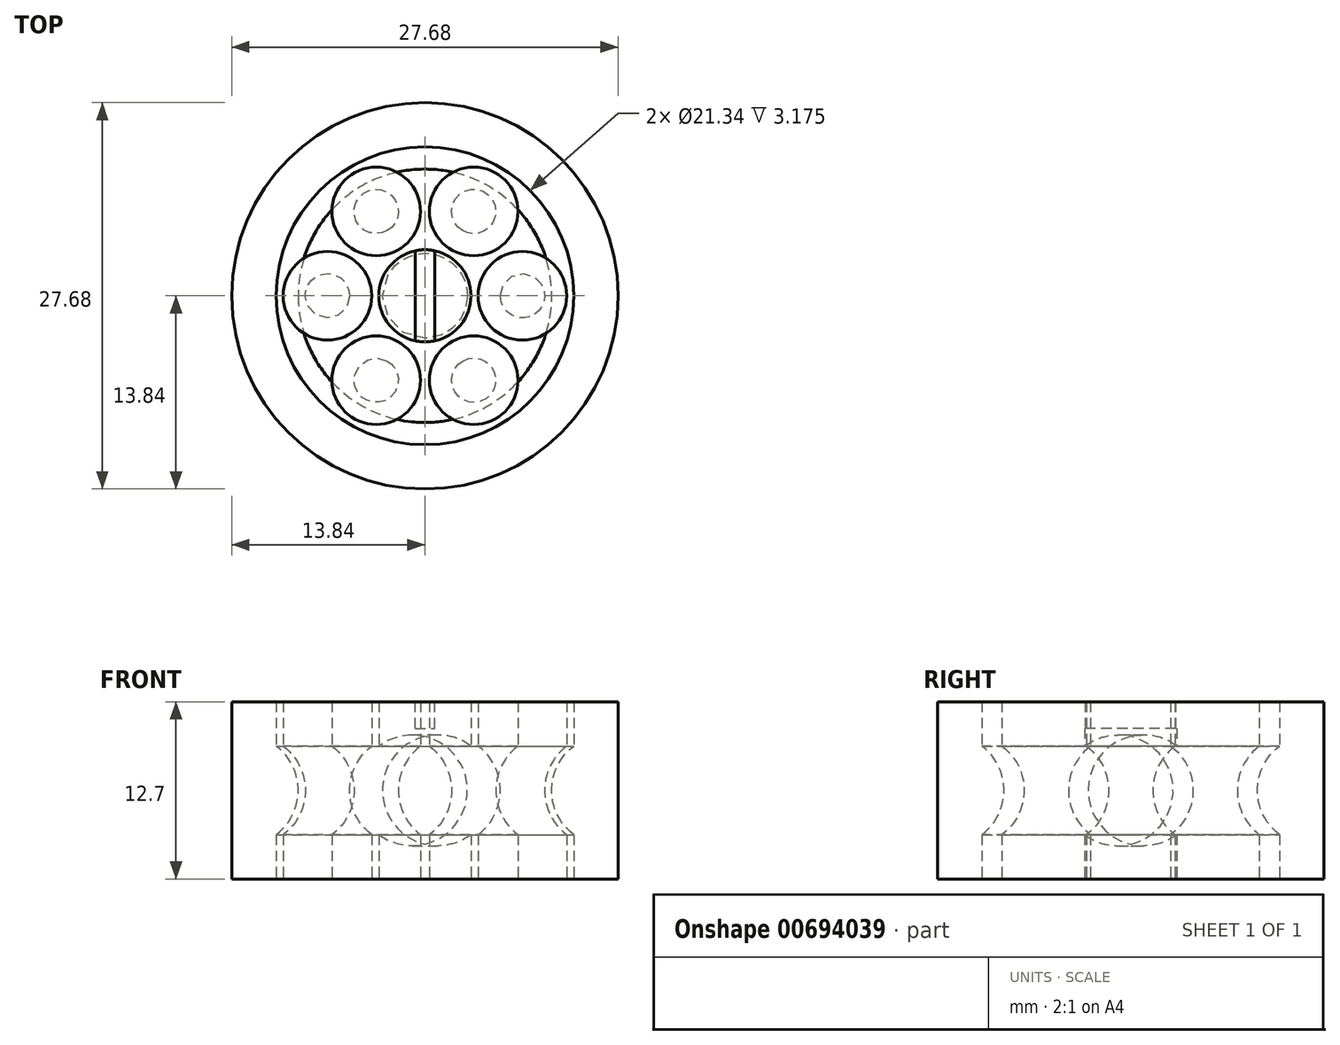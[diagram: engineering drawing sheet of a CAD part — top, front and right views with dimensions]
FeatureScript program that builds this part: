
annotation { "Feature Type Name" : "Feature", "Feature Type Description" : "" }
export const myFeature = defineFeature(function(context is Context, id is Id, definition is map)
    precondition{}
    {
        {
            var Q0;
            Q0=qCreatedBy(makeId("Front.planeOp"),FACE);
            var sketch = newSketch(context, id + "F0", { "sketchPlane" : qUnion([Q0])});
            skLineSegment(sketch, "E0.bottom", {"start": v(0, 0) * mm, "end": v(3.3, 0) * mm});
            skLineSegment(sketch, "E0.top", {"start": v(0, 12.7) * mm, "end": v(3.3, 12.7) * mm});
            skLineSegment(sketch, "E0.left", {"start": v(0, 0) * mm, "end": v(0, 12.7) * mm});
            skLineSegment(sketch, "E0.right", {"start": v(3.81, 0) * mm, "end": v(3.8, 3.18) * mm});
            skLineSegment(sketch, "E1", {"start": v(3.81, 0) * mm, "end": v(6.99, 0) * mm});
            skLineSegment(sketch, "E2", {"start": v(6.99, 0) * mm, "end": v(6.99, 12.7) * mm});
            skLineSegment(sketch, "E3", {"start": v(6.99, 12.7) * mm, "end": v(10.16, 12.7) * mm});
            skLineSegment(sketch, "E4", {"start": v(10.16, 0) * mm, "end": v(10.67, 0) * mm});
            skLineSegment(sketch, "E5", {"start": v(10.67, 0) * mm, "end": v(10.67, 3.18) * mm});
            skLineSegment(sketch, "E6", {"start": v(10.67, 12.7) * mm, "end": v(13.84, 12.7) * mm});
            skLineSegment(sketch, "E7", {"start": v(13.84, 12.7) * mm, "end": v(13.84, 0) * mm});
            skLineSegment(sketch, "E8", {"start": v(13.84, 0) * mm, "end": v(10.67, 0) * mm});
            skLineSegment(sketch, "E9", {"start": v(3.3, 0) * mm, "end": v(3.3, 3.18) * mm});
            skLineSegment(sketch, "E10", {"start": v(3.8, 12.7) * mm, "end": v(6.99, 12.7) * mm});
            skArc(sketch, "E11", {"start": v(3.8, 3.18) * mm, "mid": v(5.4, 6.35) * mm, "end": v(3.8, 9.52) * mm});
            skLineSegment(sketch, "E12.trimOffspring", {"start": v(3.8, 9.53) * mm, "end": v(3.8, 12.7) * mm});
            skArc(sketch, "E13", {"start": v(3.3, 3.18) * mm, "mid": v(4.89, 6.35) * mm, "end": v(3.3, 9.53) * mm});
            skPoint(sketch, "E14.start.orphan", {"position": v(5.4, 6.35) * mm});
            skArc(sketch, "E15.MirrorCS", {"start": v(10.67, 3.18) * mm, "mid": v(9.08, 6.35) * mm, "end": v(10.67, 9.53) * mm});
            skLineSegment(sketch, "E16.trimOffspring", {"start": v(10.67, 9.53) * mm, "end": v(10.67, 12.7) * mm});
            skLineSegment(sketch, "E17.trimOffspring", {"start": v(3.3, 9.53) * mm, "end": v(3.3, 12.7) * mm});
            skSolve(sketch);
        }
        {
            var Q0;
            Q0=makeQuery(id+"F0.imprint","IMPRINT",FACE,{"disambiguationData":[TD([[makeQuery(id+"F0.imprint","IMPRINT",EDGE,{"derivedFrom":sQuery(id+"F0.wireOp",EDGE,"E1")}),1.0]])]});
            var Q1;
            Q1=sQuery(id+"F0.wireOp",EDGE,"E2");
            revolve(context, id + "F1", {"surfaceOperationType" : NewSurfaceOperationType.NEW, "entities" : qUnion([Q0]), "axis" : qUnion([Q1]), "revolveType" : RevolveType.FULL});
        }
        {
            var Q0;
            Q0=makeQuery(id+"F0.imprint","IMPRINT",FACE,{"disambiguationData":[TD([[makeQuery(id+"F0.imprint","IMPRINT",EDGE,{"derivedFrom":sQuery(id+"F0.wireOp",EDGE,"E0.bottom")}),1.0]])]});
            var Q1;
            Q1=makeQuery(id+"F0.imprint","IMPRINT",FACE,{"disambiguationData":[TD([[makeQuery(id+"F0.imprint","IMPRINT",EDGE,{"derivedFrom":sQuery(id+"F0.wireOp",EDGE,"E5")}),-1.0]])]});
            var Q2;
            Q2=sQuery(id+"F0.wireOp",EDGE,"E0.left");
            revolve(context, id + "F2", {"surfaceOperationType" : NewSurfaceOperationType.NEW, "entities" : qUnion([Q0, Q1]), "axis" : qUnion([Q2]), "revolveType" : RevolveType.FULL});
        }
        {
            var Q0;
            Q0=makeQuery(id+"F1.opRevolve","SWEPT_BODY",BODY,{"disambiguationData":[OSD([sQuery(id+"F0.wireOp",EDGE,"E1"),sQuery(id+"F0.wireOp",EDGE,"E2"),sQuery(id+"F0.wireOp",EDGE,"E10"),sQuery(id+"F0.wireOp",EDGE,"E0.right"),sQuery(id+"F0.wireOp",EDGE,"E11"),sQuery(id+"F0.wireOp",EDGE,"E12.trimOffspring")])]});
            var Q1;
            Q1=sQuery(id+"F0.wireOp",EDGE,"E0.left");
            circularPattern(context, id + "F3", {"entities" : qUnion([Q0]), "axis" : qUnion([Q1]), "angle" : 360 * degree, "instanceCount" : 6, "equalSpace" : true});
        }
        {
            var Q0;
            Q0=makeQuery(id+"F2.opRevolve","SWEPT_FACE",FACE,{"disambiguationData":[OSD([sQuery(id+"F0.wireOp",EDGE,"E0.top")])]});
            var sketch = newSketch(context, id + "F4", { "sketchPlane" : qUnion([Q0])});
            skLineSegment(sketch, "E18.bottom", {"start": v(0.7, 3.5) * mm, "end": v(-0.7, 3.5) * mm});
            skLineSegment(sketch, "E18.top", {"start": v(0.7, -3.5) * mm, "end": v(-0.7, -3.5) * mm});
            skLineSegment(sketch, "E18.left", {"start": v(0.7, 3.5) * mm, "end": v(0.7, -3.5) * mm});
            skLineSegment(sketch, "E18.right", {"start": v(-0.7, 3.5) * mm, "end": v(-0.7, -3.5) * mm});
            skPoint(sketch, "E18.middle", {"position": v(0, 0) * mm});
            skSolve(sketch);
        }
        {
            var Q0;
            {var subQ0=sQuery(id+"F4.wireOp",EDGE,"E18.left");var subQ1=makeQuery(id+"F2.opRevolve","SWEPT_EDGE",EDGE,{"disambiguationData":[OSD([sQuery(id+"F0.wireOp",EDGE,"E0.top"),sQuery(id+"F0.wireOp",EDGE,"E17.trimOffspring")])]});var subQ2=makeQuery(id+"F4.imprint","INTERSECT",VERTEX,{"disambiguationData":[OD(0.0)],"derivedFrom":[subQ1,subQ0]});Q0=makeQuery(id+"F4.imprint","IMPRINT",FACE,{"disambiguationData":[TD([[makeQuery(id+"F4.imprint","IMPRINT",EDGE,{"disambiguationData":[TD([[subQ2,-1.0]])],"derivedFrom":subQ0}),-1.0]])]});}
            extrude(context, id + "F5", {"entities" : qUnion([Q0]), "operationType" : NewBodyOperationType.REMOVE, "oppositeDirection" : true, "depth" : 1.9 * mm, "offsetDistance" : 25.4 * mm});
        }
    });
